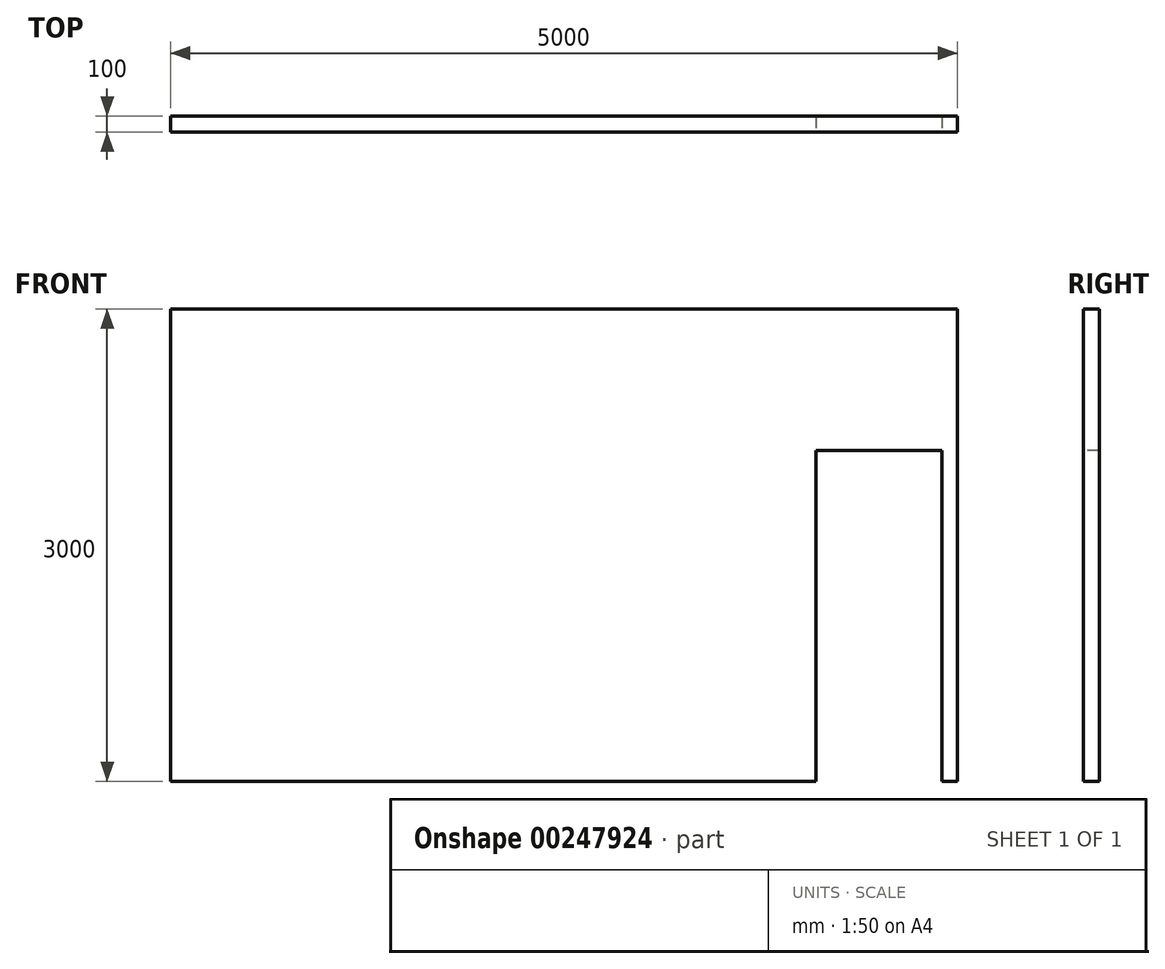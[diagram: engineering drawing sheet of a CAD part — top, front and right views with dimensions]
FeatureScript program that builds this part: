
annotation { "Feature Type Name" : "Feature", "Feature Type Description" : "" }
export const myFeature = defineFeature(function(context is Context, id is Id, definition is map)
    precondition{}
    {
        {
            var Q0;
            Q0=qCreatedBy(makeId("Front.planeOp"),FACE);
            var sketch = newSketch(context, id + "F0", { "sketchPlane" : qUnion([Q0])});
            skLineSegment(sketch, "E0.bottom", {"start": v(2500, 0) * mm, "end": v(-2500, 0) * mm});
            skLineSegment(sketch, "E0.top", {"start": v(2500, 3000) * mm, "end": v(-2500, 3000) * mm});
            skLineSegment(sketch, "E0.left", {"start": v(2500, 0) * mm, "end": v(2500, 3000) * mm});
            skLineSegment(sketch, "E0.right", {"start": v(-2500, 0) * mm, "end": v(-2500, 3000) * mm});
            skPoint(sketch, "E0.middle", {"position": v(0, 1500) * mm});
            skSolve(sketch);
        }
        {
            var Q0;
            Q0=makeQuery(id+"F0.imprint","IMPRINT",FACE,{"disambiguationData":[TD([[makeQuery(id+"F0.imprint","IMPRINT",EDGE,{"derivedFrom":sQuery(id+"F0.wireOp",EDGE,"E0.bottom")}),-1.0]])]});
            extrude(context, id + "F1", {"entities" : qUnion([Q0]), "endBound" : BoundingType.SYMMETRIC, "depth" : 100 * mm});
        }
        {
            var Q0;
            Q0=makeQuery(id+"F1.opExtrude","CAP_FACE",FACE,{"disambiguationData":[OSD([sQuery(id+"F0.wireOp",EDGE,"E0.bottom"),sQuery(id+"F0.wireOp",EDGE,"E0.top"),sQuery(id+"F0.wireOp",EDGE,"E0.left"),sQuery(id+"F0.wireOp",EDGE,"E0.right")])],"isStart":false});
            var sketch = newSketch(context, id + "F2", { "sketchPlane" : qUnion([Q0])});
            skLineSegment(sketch, "E1.bottom", {"start": v(2400, 0) * mm, "end": v(1600, 0) * mm});
            skLineSegment(sketch, "E1.top", {"start": v(2400, 2100) * mm, "end": v(1600, 2100) * mm});
            skLineSegment(sketch, "E1.left", {"start": v(2400, 0) * mm, "end": v(2400, 2100) * mm});
            skLineSegment(sketch, "E1.right", {"start": v(1600, 0) * mm, "end": v(1600, 2100) * mm});
            skPoint(sketch, "E1.middle", {"position": v(2000, 1050) * mm});
            skSolve(sketch);
        }
        {
            var Q0;
            Q0=makeQuery(id+"F2.imprint","IMPRINT",FACE,{"disambiguationData":[TD([[makeQuery(id+"F2.imprint","IMPRINT",EDGE,{"derivedFrom":sQuery(id+"F2.wireOp",EDGE,"E1.bottom")}),-1.0]])]});
            extrude(context, id + "F3", {"entities" : qUnion([Q0]), "operationType" : NewBodyOperationType.REMOVE, "endBound" : BoundingType.THROUGH_ALL, "oppositeDirection" : true, "depth" : 25 * mm});
        }
    });
